# Revit family: ROTADO_ЦокольныйДефлектор_ЦД125-200
name_source: partatom
category: Воздухораспределители
units: mm (PartAtom-declared; Revit-internal decimal feet)

## family parameters
Всегда вертикально = Да
На основе рабочей плоскости = Нет
Общий = Нет
При загрузке вырезать с полостями = Нет
Размер круглого соединителя = Использовать диаметр
Тип детали = Нормальный
Точка расчета площади = Нет

## types (3) — shared parameters
ADSK_URL документации изделия = https://rotado.ru
ADSK_URL страницы изделия = https://rotado.ru
ADSK_Версия Revit = 2019
ADSK_Единица измерения = шт.
ADSK_Завод-изготовитель = ROTADO
ADSK_Количество = 1
ADSK_Материал = ROTADO_Сталь_Нержавеющая_Оцинкованная
ADSK_Наименование = Цокольный дефлектор
ADSK_Размер_Ширина = 230 мм
URL = https://rotado.ru
d2 = 230 мм
Изготовитель = ROTADO
Производитель_Контакты_Телефон = 88007002460

## per-type parameters (varying)
| type | ADSK_Марка | ADSK_Масса | ADSK_Масса_Текст | ADSK_Обозначение | ADSK_Размер_Диаметр | D | D1 | R | d1 | h | h1 |
| ЦД_160 | ЦД ROTADO 160 | 8 | 8 | ЦД ROTADO 160 | 160 мм | 160 мм | 158 мм | 80 мм | 170 мм | 549 мм | 160 мм |
| ЦД_200 | ЦД ROTADO 160 | 10 | 10 | ЦД ROTADO 160 | 200 мм | 200 мм | 198 мм | 100 мм | 210 мм | 459 мм | 200 мм |
| ЦД_125 | ЦД ROTADO 125 | 5 | 5 | ЦД ROTADO 125 | 125 мм | 125 мм | 123 мм | 63 мм | 135 мм | 549 мм | 125 мм |
